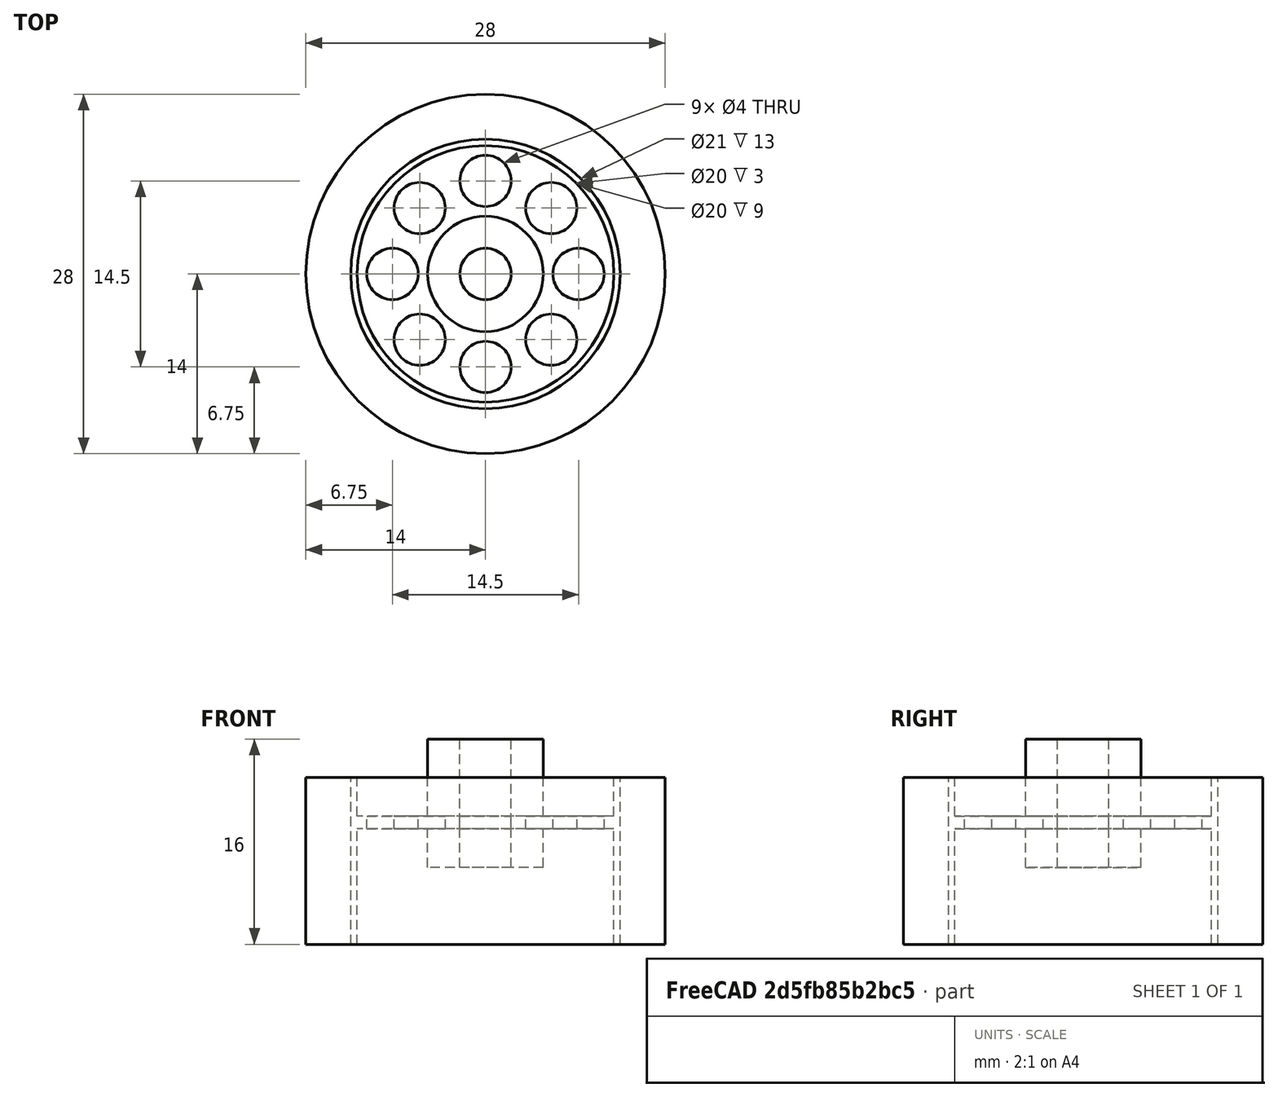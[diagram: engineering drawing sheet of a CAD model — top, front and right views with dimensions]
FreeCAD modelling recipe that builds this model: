
FCSTD DOCUMENT  (FreeCAD 0.14R3702 (Git))
Label: drivewheel
License: CC-BY 3.0
LicenseURL: http://creativecommons.org/licenses/by/3.0/
objects: Part::Cylinder×12, Part::Cut×5, Part::MultiFuse×4, Part::Compound×1
note: 22 computed .brp shape members not serialized (recipe doc carries the construction recipe); baked Part::Feature solids carry a one-line shape summary decoded from their .brp

FEATURE [Part::Cylinder] Cylinder
  Angle = 360
  Height = 1
  Radius = 10
FEATURE [Part::Cylinder] Cylinder001
  Angle = 360
  Height = 10
  Placement = pos=(0,7.25,0) rot=(0,0,1;1.5708rad)
  Radius = 2
FEATURE [Part::Cylinder] Cylinder002
  Angle = 360
  Height = 10
  Radius = 4.5
FEATURE [Part::Cylinder] Cylinder003
  Angle = 360
  Height = 10
  Placement = pos=(7.25,0,0) rot=(0,0,1;0.017453rad)
  Radius = 2
FEATURE [Part::Cylinder] Cylinder004
  Angle = 360
  Height = 10
  Placement = pos=(-7.25,0,0) rot=(0,0,1;1.5708rad)
  Radius = 2
FEATURE [Part::Cylinder] Cylinder005
  Angle = 360
  Height = 10
  Placement = pos=(0,-7.25,0) rot=(0,0,1;1.5708rad)
  Radius = 2
FEATURE [Part::MultiFuse] Fusion
  Shapes = -> [Cylinder001,Cylinder005,Cylinder004,Cylinder003]
FEATURE [Part::MultiFuse] Fusion002
  Placement = pos=(0,0,-5) rot=(0,0,1;0rad)
  Shapes = -> [Fusion]
FEATURE [Part::Cylinder] Cylinder010
  Angle = 360
  Height = 13
  Placement = pos=(0,0,-6) rot=(0,0,1;0rad)
  Radius = 10
FEATURE [Part::Cylinder] Cylinder011
  Angle = 360
  Height = 13
  Placement = pos=(0,0,-6) rot=(0,0,1;0rad)
  Radius = 14
FEATURE [Part::Cylinder] Cylinder012
  Angle = 360
  Height = 13
  Placement = pos=(0,0,-6) rot=(0,0,1;0rad)
  Radius = 10.5
FEATURE [Part::Cut] Cut
  Base = -> Cylinder011
  Tool = -> Cylinder012
FEATURE [Part::Cylinder] Cylinder013
  Angle = 360
  Height = 13
  Placement = pos=(0,0,-6) rot=(0,0,1;0rad)
  Radius = 10.5
FEATURE [Part::Cut] Cut001
  Base = -> Cylinder013
  Tool = -> Cylinder010
FEATURE [Part::Cylinder] Cylinder014
  Angle = 360
  Height = 10
  Radius = 4.5
FEATURE [Part::Cut] Cut002
  Base = -> Cylinder
  Tool = -> Cylinder002
FEATURE [Part::Cut] Cut003
  Base = -> Cut002
  Placement = pos=(0,0,3) rot=(0,0,1;0rad)
  Tool = -> Fusion002
FEATURE [Part::MultiFuse] Fusion004
  Shapes = -> [Cut003,Cut001]
FEATURE [Part::Cylinder] Cylinder015
  Angle = 360
  Height = 10
  Radius = 2
FEATURE [Part::Cut] Cut004
  Base = -> Cylinder014
  Tool = -> Cylinder015
FEATURE [Part::MultiFuse] Fusion005
  Shapes = -> [Cut004,Fusion004]
FEATURE [Part::Compound] Compound  label="DriveWheel"
  Links = -> [Cut,Fusion005]
